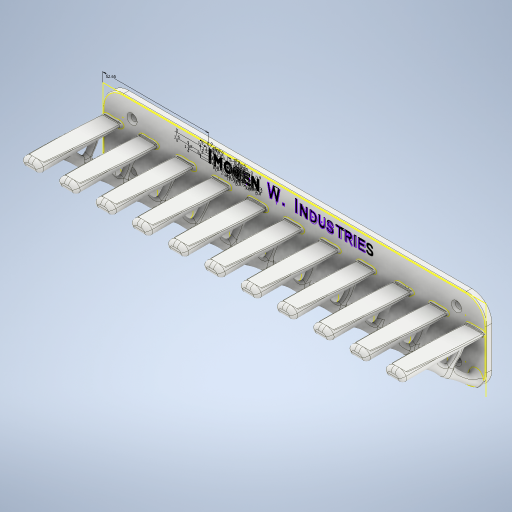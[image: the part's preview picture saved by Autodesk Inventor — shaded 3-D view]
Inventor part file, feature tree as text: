
AUTODESK INVENTOR PART (.ipt)
format: ipt  version: 2023 (Build 270158030, 158C)  size: 3,747,840 bytes
history: native  units: mm
features: fillet x2, sketch x2, hole x1, projected_geometry x1
ambient origin geometry x8: Origin, YZ Plane, XZ Plane, XY Plane, X Axis, Y Axis, Z Axis, Center Point
bodies: Solid1 (feature_tree), Body80 (feature_tree)
feature tree (6):
  fillet  "Fillet1"  Radius=10.0mm
  fillet  "Fillet2"  Radius=0.5mm
  hole  "Hole1"  [1 undecoded]
  sketch  "Sketch1"  dims[d5=5.0mm d6=8.0mm]
  projected_geometry  "Projected Loop1"
  sketch  "Sketch2"  dims[d7=8.0mm d8=14.0mm d9=14.0mm d10=3.0mm d11=10.0mm d12=5.0mm d13=1.0mm d14=90.0deg d15=8.0mm d16=20.594885mm d17=1.5mm d18=6.1mm d19=0.9mm d20=1.1mm d21=0.9mm d22=1.45mm d23=52.65mm d24=3.2mm d25=1.0mm d26=1.0mm d27=2.05mm d28=0.9mm d29=2.3mm d30=2.45mm d31=0.0mm d32=2.9mm d33=1.9mm d34=1.0mm d35=1.58mm d36=2.5mm d37=0.8mm d38=0.8mm d39=2.5mm d40=0.85mm d41=6.25mm d42=1.75mm d43=0.9mm d44=0.87mm d45=1.3mm d46=0.6mm d47=0.8mm d48=3.45mm d49=2.2mm d50=0.9mm d51=2.3mm d52=2.25mm d53=1.45mm d54=0.4mm d55=0.05mm d56=0.36mm d57=1.1mm d58=1.83mm d59=1.47mm d60=0.3mm d61=0.6mm d62=1.34mm d63=0.56mm d64=0.93mm d65=0.59mm d66=0.6mm d67=0.955mm d68=1.705715mm d69=0.383117mm d70=0.798998mm d71=2.712931mm d72=0.189198mm d73=0.174232mm d74=0.052554mm d75=0.391128mm d76=0.332214mm d77=0.491457mm d78=0.113416mm d79=1.25mm d80=0.85mm d81=3.33mm d82=0.95mm d83=1.4mm d84=0.85mm d85=0.92mm d86=0.1mm d87=0.9mm d88=0.88mm d89=2.0mm d90=0.8mm d92=0.9mm d93=2.0mm]
note: 1 required parameter value undecoded (feature->parameter linkage not recoverable at this tier; creation-order binding heuristic only, values carry confidence <= 0.55)
